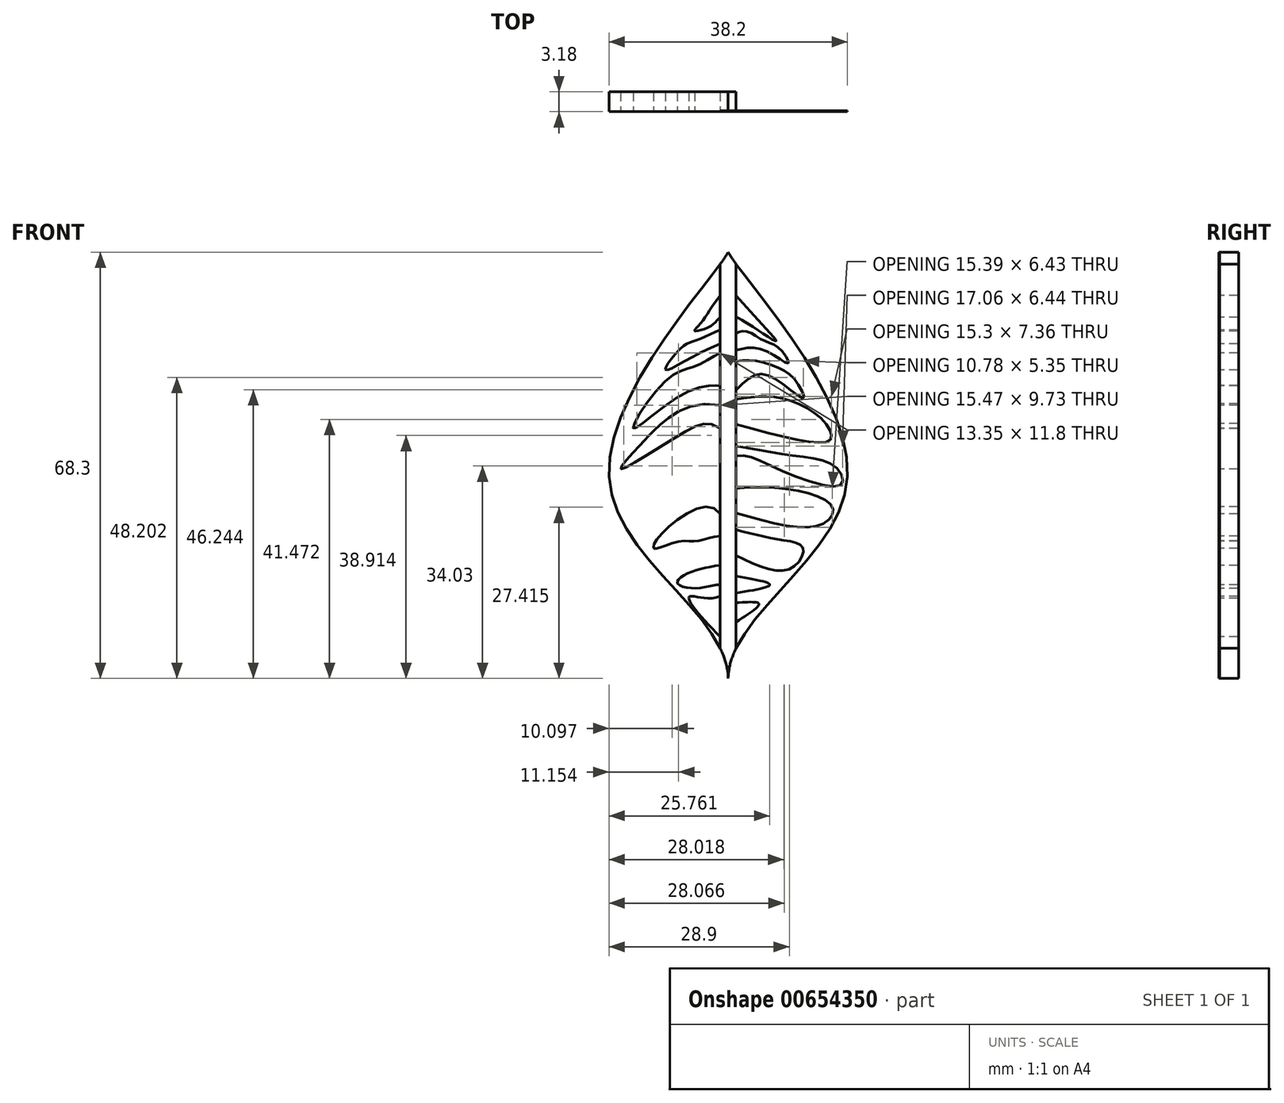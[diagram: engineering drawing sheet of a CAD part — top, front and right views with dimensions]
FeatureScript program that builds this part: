
annotation { "Feature Type Name" : "Feature", "Feature Type Description" : "" }
export const myFeature = defineFeature(function(context is Context, id is Id, definition is map)
    precondition{}
    {
        {
            var Q0;
            Q0=qCreatedBy(makeId("Front.planeOp"),FACE);
            var sketch = newSketch(context, id + "F0", { "sketchPlane" : qUnion([Q0])});
            skFitSpline(sketch, "E0", {"points": [v(0, 68.3) * mm, v(-19.05, 31.86) * mm, v(0, 0) * mm], "startDerivative": vector(-16.32, -28.97) * mm, "endDerivative": vector(1.15, -64.12) * mm});
            skFitSpline(sketch, "E1.MirrorCS", {"points": [v(0, 68.3) * mm, v(19.05, 31.86) * mm, v(0, 0) * mm], "startDerivative": vector(16.32, -28.97) * mm, "endDerivative": vector(-1.15, -64.12) * mm});
            skLineSegment(sketch, "E2", {"start": v(-1.27, 66.4) * mm, "end": v(-1.27, 4.82) * mm});
            skLineSegment(sketch, "E3.MirrorCS", {"start": v(1.27, 66.4) * mm, "end": v(1.27, 4.82) * mm});
            skPoint(sketch, "E4", {"position": v(-11.17, 53) * mm});
            skFitSpline(sketch, "E5", {"points": [v(-1.27, 61.34) * mm, v(-4.47, 56.8) * mm, v(-5.34, 55.7) * mm, v(-2.69, 56.5) * mm, v(-1.27, 57.88) * mm], "startDerivative": vector(-11.65, -13.8) * mm, "endDerivative": vector(6.73, 5.6) * mm});
            skFitSpline(sketch, "E6", {"points": [v(-1.27, 55.84) * mm, v(-5.43, 54.06) * mm, v(-7.36, 53.1) * mm, v(-10.05, 49.47) * mm, v(-1.27, 53.61) * mm], "startDerivative": vector(-18.1, -7.86) * mm, "endDerivative": vector(34.04, 12.72) * mm});
            skFitSpline(sketch, "E7", {"points": [v(-1.27, 52.14) * mm, v(-5.34, 49.98) * mm, v(-9.64, 48.01) * mm, v(-15.2, 40.06) * mm, v(-6.66, 45.87) * mm, v(-1.27, 46.88) * mm], "startDerivative": vector(-19.6, -9.24) * mm, "endDerivative": vector(10.83, -0.57) * mm});
            skFitSpline(sketch, "E8", {"points": [v(-1.27, 43.78) * mm, v(-11.7, 39.87) * mm, v(-14.4, 37.05) * mm, v(-17.19, 33.59) * mm, v(-7.33, 39.29) * mm, v(-1.27, 40.1) * mm], "startDerivative": vector(-60.5, 12.61) * mm, "endDerivative": vector(32.85, -21.08) * mm});
            skFitSpline(sketch, "E9", {"points": [v(-1.27, 26.38) * mm, v(-10.44, 23.42) * mm, v(-11.82, 20.83) * mm, v(-8.16, 21.9) * mm, v(-4.9, 22.02) * mm, v(-1.27, 22.81) * mm], "startDerivative": vector(-18.7, 29.6) * mm, "endDerivative": vector(22.6, 1.14) * mm});
            skFitSpline(sketch, "E10", {"points": [v(-1.27, 18.14) * mm, v(-6.54, 16.82) * mm, v(-8.14, 15.29) * mm, v(-5.27, 14.45) * mm, v(-1.27, 15) * mm], "startDerivative": vector(-18.56, -2.64) * mm, "endDerivative": vector(14.38, -0.3) * mm});
            skFitSpline(sketch, "E11", {"points": [v(-1.27, 13.13) * mm, v(-6.25, 13.08) * mm, v(-1.27, 6.66) * mm], "startDerivative": vector(-15.15, -5.29) * mm, "endDerivative": vector(14.56, -14.61) * mm});
            skFitSpline(sketch, "E12", {"points": [v(1.27, 61.33) * mm, v(5.39, 56.79) * mm, v(7.66, 54.05) * mm, v(3.99, 56.32) * mm, v(1.27, 57.93) * mm], "startDerivative": vector(12.87, -14.38) * mm, "endDerivative": vector(-10.47, 5.63) * mm});
            skFitSpline(sketch, "E13", {"points": [v(1.27, 55.24) * mm, v(2.79, 55.65) * mm, v(5.64, 54.15) * mm, v(8.18, 52.9) * mm, v(9.63, 50.53) * mm, v(5.75, 52.6) * mm, v(1.27, 52.6) * mm], "startDerivative": vector(9.36, 6.7) * mm, "endDerivative": vector(-20.91, -5.04) * mm});
            skFitSpline(sketch, "E14", {"points": [v(1.27, 50.84) * mm, v(4.61, 50.84) * mm, v(8.7, 49.47) * mm, v(11.03, 47.42) * mm, v(12.11, 44.94) * mm, v(9.16, 46.85) * mm, v(4.92, 48.77) * mm, v(1.27, 46.18) * mm], "startDerivative": vector(23.51, 2) * mm, "endDerivative": vector(-22.57, -23.14) * mm});
            skFitSpline(sketch, "E15", {"points": [v(1.27, 44.73) * mm, v(7.66, 45.04) * mm, v(14.75, 41.78) * mm, v(16.4, 38.27) * mm, v(1.27, 40.7) * mm], "startDerivative": vector(27.5, 4.21) * mm, "endDerivative": vector(-60.08, 16.52) * mm});
            skFitSpline(sketch, "E16", {"points": [v(1.27, 37.25) * mm, v(11.21, 35.6) * mm, v(17.32, 33.76) * mm, v(18.1, 31.05) * mm, v(7.66, 33.67) * mm, v(1.27, 35.61) * mm], "startDerivative": vector(42.6, -7.8) * mm, "endDerivative": vector(-27.67, -7.78) * mm});
            skFitSpline(sketch, "E17", {"points": [v(1.27, 30.44) * mm, v(9.47, 30.36) * mm, v(16.7, 27.39) * mm, v(14.79, 24.6) * mm, v(1.27, 26.52) * mm], "startDerivative": vector(29.83, 2.06) * mm, "endDerivative": vector(-48.14, 13.88) * mm});
            skFitSpline(sketch, "E18", {"points": [v(1.27, 23.8) * mm, v(8.33, 22.24) * mm, v(12, 20.84) * mm, v(9.81, 17.53) * mm, v(1.27, 19.7) * mm], "startDerivative": vector(25.57, -6.38) * mm, "endDerivative": vector(-30.9, 15.13) * mm});
            skFitSpline(sketch, "E19", {"points": [v(1.27, 16.4) * mm, v(6.67, 15) * mm, v(1.27, 13.69) * mm], "startDerivative": vector(16.2, -2.8) * mm, "endDerivative": vector(-16.21, -2.6) * mm});
            skFitSpline(sketch, "E20", {"points": [v(1.27, 12.12) * mm, v(4.92, 11.94) * mm, v(1.27, 9.06) * mm], "startDerivative": vector(11.21, 0.82) * mm, "endDerivative": vector(-10.77, -6.77) * mm});
            skSolve(sketch);
        }
        {
            var Q0;
            {var subQ5=sQuery(id+"F0.wireOp",EDGE,"E5");Q0=makeQuery(id+"F0.imprint","IMPRINT",FACE,{"disambiguationData":[TD([[makeQuery(id+"F0.imprint","IMPRINT",EDGE,{"derivedFrom":subQ5}),-1.0]])]});}
            var Q1;
            {var subQ4=sQuery(id+"F0.wireOp",EDGE,"E1.MirrorCS");var subQ7=sQuery(id+"F0.wireOp",EDGE,"E0");var subQ23=makeQuery(id+"F0.imprint","INTERSECT",VERTEX,{"disambiguationData":[OD(0.0)],"derivedFrom":[subQ7,subQ4]});Q1=makeQuery(id+"F0.imprint","IMPRINT",FACE,{"disambiguationData":[TD([[makeQuery(id+"F0.imprint","IMPRINT",EDGE,{"disambiguationData":[TD([[subQ23,-1.0]])],"derivedFrom":subQ7}),1.0]])]});}
            extrude(context, id + "F1", {"entities" : qUnion([Q0, Q1]), "depth" : -3.17 * mm, "offsetDistance" : 25.4 * mm});
        }
        {
            var Q0;
            {var subQ9=sQuery(id+"F0.wireOp",EDGE,"E0");var subQ12=sQuery(id+"F0.wireOp",EDGE,"E1.MirrorCS");var subQ13=makeQuery(id+"F0.imprint","INTERSECT",VERTEX,{"disambiguationData":[OD(0.0)],"derivedFrom":[subQ9,subQ12]});Q0=makeQuery(id+"F0.imprint","IMPRINT",FACE,{"disambiguationData":[TD([[makeQuery(id+"F0.imprint","IMPRINT",EDGE,{"disambiguationData":[TD([[subQ13,-1.0]])],"derivedFrom":subQ9}),1.0]])]});}
            var Q1;
            {var subQ3=sQuery(id+"F0.wireOp",EDGE,"bc2e5532-e3e4-466e-9dad-cbe47fc49d54");Q1=makeQuery(id+"F0.imprint","IMPRINT",FACE,{"disambiguationData":[TD([[makeQuery(id+"F0.imprint","IMPRINT",EDGE,{"derivedFrom":subQ3}),-1.0]])]});}
            var Q2;
            {var subQ0=sQuery(id+"F0.wireOp",EDGE,"E3.MirrorCS");var subQ1=sQuery(id+"F0.wireOp",EDGE,"E1.MirrorCS");var subQ2=makeQuery(id+"F0.imprint","INTERSECT",VERTEX,{"disambiguationData":[OD(0.0)],"derivedFrom":[subQ1,subQ0]});Q2=makeQuery(id+"F0.imprint","IMPRINT",FACE,{"disambiguationData":[TD([[makeQuery(id+"F0.imprint","IMPRINT",EDGE,{"disambiguationData":[TD([[subQ2,-1.0]])],"derivedFrom":subQ1}),-1.0]])]});}
            extrude(context, id + "F2", {"entities" : qUnion([Q0, Q1, Q2]), "depth" : (-(1 / 8)) * mm, "offsetDistance" : 25.4 * mm});
        }
    });
